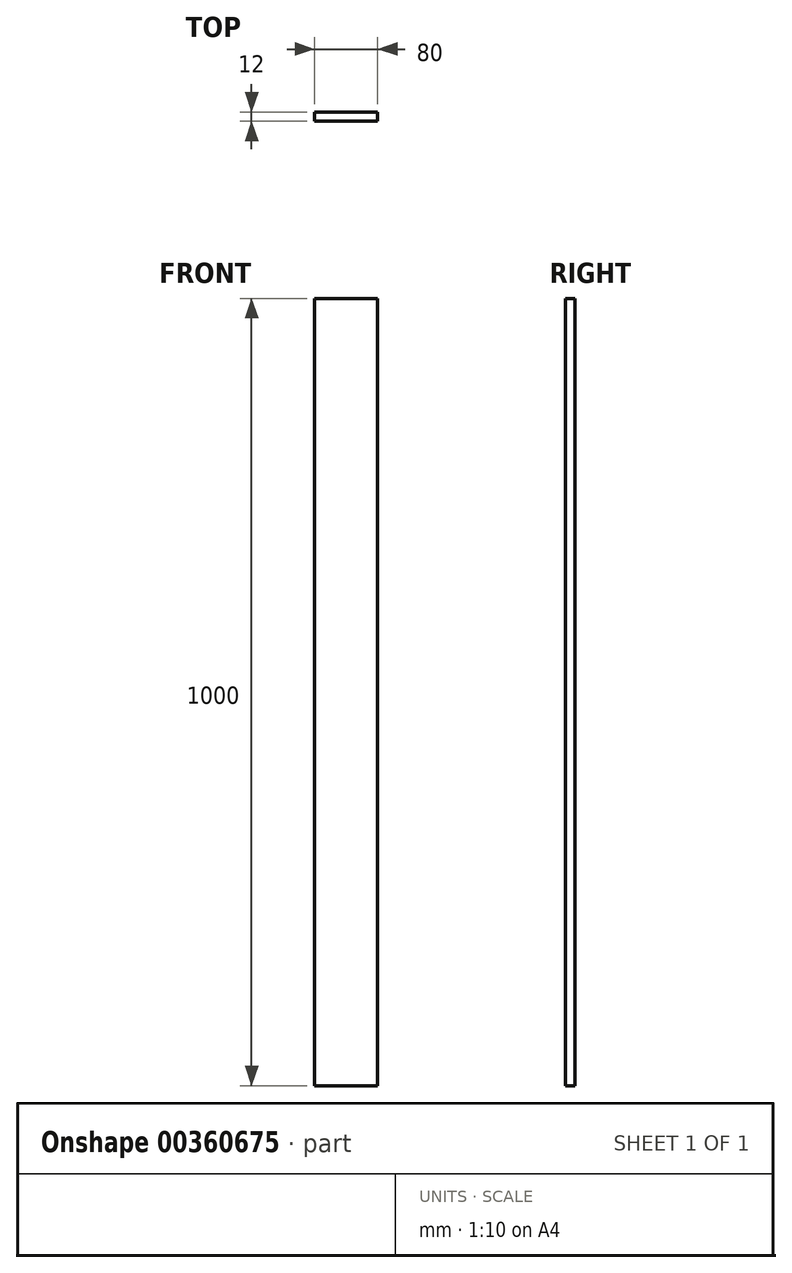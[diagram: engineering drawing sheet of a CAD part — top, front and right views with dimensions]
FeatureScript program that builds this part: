
annotation { "Feature Type Name" : "Feature", "Feature Type Description" : "" }
export const myFeature = defineFeature(function(context is Context, id is Id, definition is map)
    precondition{}
    {
        {
            var Q0;
            Q0=qCreatedBy(makeId("Front.planeOp"),FACE);
            var sketch = newSketch(context, id + "F0", { "sketchPlane" : qUnion([Q0])});
            skLineSegment(sketch, "E0.bottom", {"start": v(0, 0) * mm, "end": v(80, 0) * mm});
            skLineSegment(sketch, "E0.top", {"start": v(0, 1000) * mm, "end": v(80, 1000) * mm});
            skLineSegment(sketch, "E0.left", {"start": v(0, 0) * mm, "end": v(0, 1000) * mm});
            skLineSegment(sketch, "E0.right", {"start": v(80, 0) * mm, "end": v(80, 1000) * mm});
            skSolve(sketch);
        }
        {
            var Q0;
            Q0=makeQuery(id+"F0.imprint","IMPRINT",FACE,{"disambiguationData":[TD([[makeQuery(id+"F0.imprint","IMPRINT",EDGE,{"derivedFrom":sQuery(id+"F0.wireOp",EDGE,"E0.bottom")}),1.0]])]});
            extrude(context, id + "F1", {"entities" : qUnion([Q0]), "depth" : 12 * mm});
        }
    });
